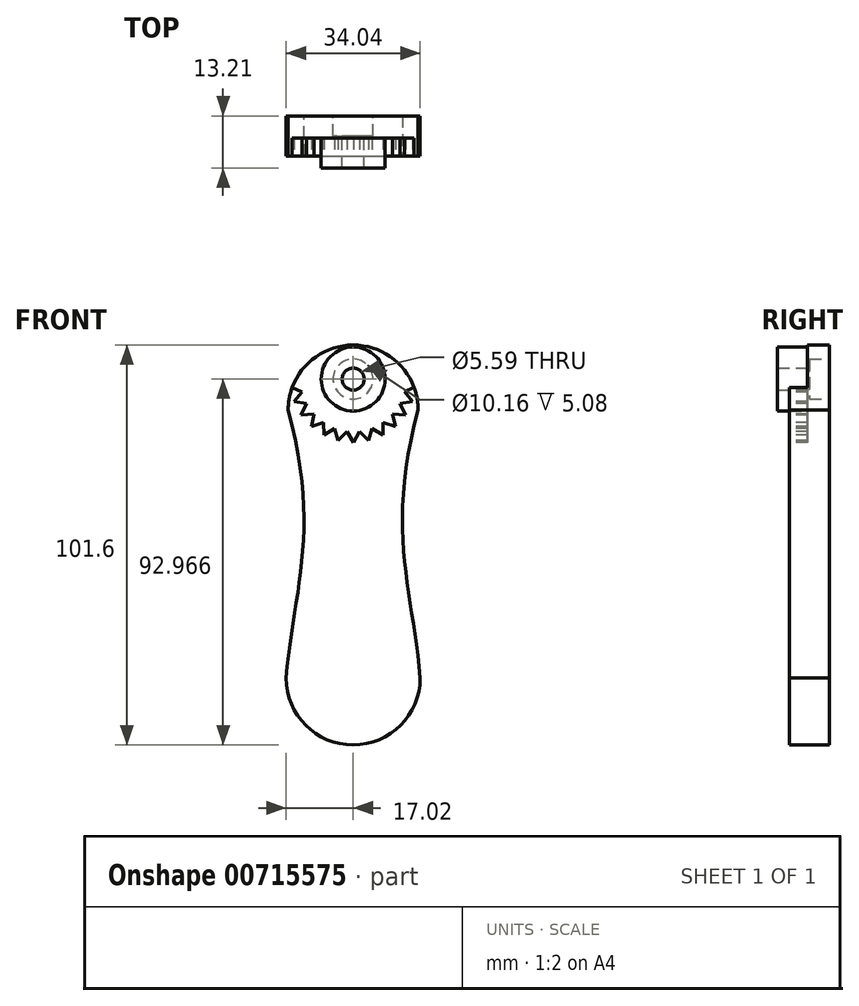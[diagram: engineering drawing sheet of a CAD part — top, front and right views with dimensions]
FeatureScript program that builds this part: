
annotation { "Feature Type Name" : "Feature", "Feature Type Description" : "" }
export const myFeature = defineFeature(function(context is Context, id is Id, definition is map)
    precondition{}
    {
        {
            var Q0;
            Q0=qCreatedBy(makeId("Front.planeOp"),FACE);
            var sketch = newSketch(context, id + "F0", { "sketchPlane" : qUnion([Q0])});
            skArc(sketch, "E0", {"start": v(16.51, 16.2) * mm, "mid": v(0, 32.71) * mm, "end": v(-16.51, 16.2) * mm});
            skArc(sketch, "E1", {"start": v(-17.02, -51.87) * mm, "mid": v(0, -68.89) * mm, "end": v(17.02, -51.87) * mm});
            skPoint(sketch, "E2", {"position": v(0, 32.71) * mm});
            skPoint(sketch, "E3", {"position": v(0, -68.89) * mm});
            skFitSpline(sketch, "E4", {"points": [v(-16.51, 16.2) * mm, v(-17.02, -51.87) * mm], "startDerivative": vector(24.94, -92.74) * mm, "endDerivative": vector(-5.66, -67.8) * mm});
            skFitSpline(sketch, "E5.MirrorCS", {"points": [v(16.51, 16.2) * mm, v(17.02, -51.87) * mm], "startDerivative": vector(-24.94, -92.74) * mm, "endDerivative": vector(5.66, -67.8) * mm});
            skLineSegment(sketch, "E6", {"start": v(-12.7, -17.82) * mm, "end": v(12.7, -17.82) * mm, "construction": true});
            skSolve(sketch);
        }
        {
            var Q0;
            Q0=makeQuery(id+"F0.imprint","IMPRINT",FACE,{"disambiguationData":[TD([[makeQuery(id+"F0.imprint","IMPRINT",EDGE,{"derivedFrom":sQuery(id+"F0.wireOp",EDGE,"E0")}),1.0]])]});
            extrude(context, id + "F1", {"entities" : qUnion([Q0]), "depth" : 10.16 * mm, "offsetDistance" : 25.4 * mm});
        }
        {
            var Q0;
            Q0=makeQuery(id+"F1.opExtrude","CAP_FACE",FACE,{"disambiguationData":[OSD([sQuery(id+"F0.wireOp",EDGE,"E0"),sQuery(id+"F0.wireOp",EDGE,"E1"),sQuery(id+"F0.wireOp",EDGE,"E4"),sQuery(id+"F0.wireOp",EDGE,"E5.MirrorCS")])],"isStart":false});
            var sketch = newSketch(context, id + "F2", { "sketchPlane" : qUnion([Q0])});
            skLineSegment(sketch, "E7", {"start": v(0, 32.71) * mm, "end": v(0, 24.08) * mm, "construction": true});
            skCircle(sketch, "E8", {"center": v(0, 24.08) * mm, "radius": 2.8 * mm});
            skCircle(sketch, "E9", {"center": v(0, 24.08) * mm, "radius": 8.13 * mm});
            skSolve(sketch);
        }
        {
            var Q0;
            Q0=makeQuery(id+"F2.imprint","IMPRINT",FACE,{"disambiguationData":[TD([[makeQuery(id+"F2.imprint","IMPRINT",EDGE,{"derivedFrom":sQuery(id+"F2.wireOp",EDGE,"E8")}),-1.0]])]});
            extrude(context, id + "F3", {"entities" : qUnion([Q0]), "operationType" : NewBodyOperationType.ADD, "depth" : 3.05 * mm, "offsetDistance" : 25.4 * mm});
        }
        {
            var Q0;
            Q0=makeQuery(id+"F3.boolean.opBoolean","SPLIT",FACE,{"disambiguationData":[TD([makeQuery(id+"F3.opExtrude","SWEPT_FACE",FACE,{"disambiguationData":[OSD([sQuery(id+"F2.wireOp",EDGE,"E8")])]})])],"derivedFrom":makeQuery(id+"F1.opExtrude","CAP_FACE",FACE,{"disambiguationData":[OSD([sQuery(id+"F0.wireOp",EDGE,"E0"),sQuery(id+"F0.wireOp",EDGE,"E1"),sQuery(id+"F0.wireOp",EDGE,"E4"),sQuery(id+"F0.wireOp",EDGE,"E5.MirrorCS")])],"isStart":false})});
            extrude(context, id + "F4", {"entities" : qUnion([Q0]), "operationType" : NewBodyOperationType.REMOVE, "endBound" : BoundingType.SYMMETRIC, "oppositeDirection" : true, "depth" : 101.6 * mm, "offsetDistance" : 25.4 * mm});
        }
        {
            var Q0;
            {var subQ0=sQuery(id+"F0.wireOp",EDGE,"E4");var subQ1=sQuery(id+"F0.wireOp",EDGE,"E1");var subQ2=sQuery(id+"F0.wireOp",EDGE,"E5.MirrorCS");var subQ3=sQuery(id+"F0.wireOp",EDGE,"E0");Q0=makeQuery(id+"F3.boolean.opBoolean","SPLIT",FACE,{"disambiguationData":[TD([makeQuery(id+"F1.opExtrude","SWEPT_FACE",FACE,{"disambiguationData":[OSD([subQ3])]})])],"derivedFrom":makeQuery(id+"F1.opExtrude","CAP_FACE",FACE,{"disambiguationData":[OSD([subQ3,subQ1,subQ0,subQ2])],"isStart":false})});}
            var sketch = newSketch(context, id + "F5", { "sketchPlane" : qUnion([Q0])});
            skLineSegment(sketch, "E10", {"start": v(0, 24.08) * mm, "end": v(0, 0) * mm, "construction": true});
            skLineSegment(sketch, "E11", {"start": v(-15.97, 22.08) * mm, "end": v(-12.93, 20.8) * mm});
            skLineSegment(sketch, "E12.1.0", {"start": v(-12.95, 20.88) * mm, "end": v(-15.03, 18.32) * mm});
            skLineSegment(sketch, "E12.1.1", {"start": v(-15.03, 18.32) * mm, "end": v(-11.77, 17.8) * mm});
            skLineSegment(sketch, "E12.2.0", {"start": v(-11.8, 17.88) * mm, "end": v(-13.21, 14.9) * mm});
            skLineSegment(sketch, "E12.2.1", {"start": v(-13.21, 14.9) * mm, "end": v(-9.92, 15.17) * mm});
            skLineSegment(sketch, "E12.3.0", {"start": v(-9.98, 15.23) * mm, "end": v(-10.63, 12) * mm});
            skLineSegment(sketch, "E12.3.1", {"start": v(-10.63, 12) * mm, "end": v(-7.5, 13.05) * mm});
            skLineSegment(sketch, "E12.4.0", {"start": v(-7.58, 13.1) * mm, "end": v(-7.43, 9.8) * mm});
            skLineSegment(sketch, "E12.4.1", {"start": v(-7.43, 9.8) * mm, "end": v(-4.65, 11.58) * mm});
            skLineSegment(sketch, "E12.5.0", {"start": v(-4.73, 11.6) * mm, "end": v(-3.8, 8.44) * mm});
            skLineSegment(sketch, "E12.5.1", {"start": v(-3.8, 8.44) * mm, "end": v(-1.52, 10.83) * mm});
            skLineSegment(sketch, "E12.6.0", {"start": v(-1.6, 10.84) * mm, "end": v(0.05, 7.98) * mm});
            skLineSegment(sketch, "E12.6.1", {"start": v(0.05, 7.98) * mm, "end": v(1.7, 10.85) * mm});
            skLineSegment(sketch, "E12.7.0", {"start": v(1.6, 10.84) * mm, "end": v(3.9, 8.46) * mm});
            skLineSegment(sketch, "E12.7.1", {"start": v(3.9, 8.46) * mm, "end": v(4.81, 11.64) * mm});
            skLineSegment(sketch, "E12.8.0", {"start": v(4.73, 11.6) * mm, "end": v(7.53, 9.85) * mm});
            skLineSegment(sketch, "E12.8.1", {"start": v(7.53, 9.85) * mm, "end": v(7.65, 13.15) * mm});
            skLineSegment(sketch, "E12.9.0", {"start": v(7.58, 13.1) * mm, "end": v(10.71, 12.07) * mm});
            skLineSegment(sketch, "E12.9.1", {"start": v(10.71, 12.07) * mm, "end": v(10.04, 15.3) * mm});
            skLineSegment(sketch, "E12.10.0", {"start": v(9.98, 15.23) * mm, "end": v(13.27, 14.98) * mm});
            skLineSegment(sketch, "E12.10.1", {"start": v(13.27, 14.98) * mm, "end": v(11.85, 17.96) * mm});
            skLineSegment(sketch, "E12.11.0", {"start": v(11.8, 17.88) * mm, "end": v(15.07, 18.42) * mm});
            skLineSegment(sketch, "E12.11.1", {"start": v(15.07, 18.42) * mm, "end": v(12.97, 20.97) * mm});
            skLineSegment(sketch, "E12.12.0", {"start": v(12.95, 20.88) * mm, "end": v(15.98, 22.19) * mm});
            skPoint(sketch, "E12.center", {"position": v(0, 24.08) * mm});
            skArc(sketch, "E13.trimOffspring", {"start": v(-13.33, 24.08) * mm, "mid": v(-13.33, 24.03) * mm, "end": v(-13.33, 23.99) * mm});
            skArc(sketch, "E14.trimOffspring", {"start": v(-12.95, 20.88) * mm, "mid": v(-12.94, 20.84) * mm, "end": v(-12.93, 20.8) * mm});
            skArc(sketch, "E15.trimOffspring", {"start": v(-11.8, 17.88) * mm, "mid": v(-11.79, 17.84) * mm, "end": v(-11.77, 17.8) * mm});
            skArc(sketch, "E16.trimOffspring", {"start": v(-9.98, 15.23) * mm, "mid": v(-9.95, 15.2) * mm, "end": v(-9.92, 15.17) * mm});
            skArc(sketch, "E17.trimOffspring", {"start": v(-7.58, 13.1) * mm, "mid": v(-7.54, 13.08) * mm, "end": v(-7.5, 13.05) * mm});
            skArc(sketch, "E18.trimOffspring", {"start": v(-4.73, 11.6) * mm, "mid": v(-4.69, 11.6) * mm, "end": v(-4.65, 11.58) * mm});
            skArc(sketch, "E19.trimOffspring", {"start": v(-1.6, 10.84) * mm, "mid": v(-1.56, 10.83) * mm, "end": v(-1.52, 10.83) * mm});
            skArc(sketch, "E20.trimOffspring", {"start": v(1.6, 10.84) * mm, "mid": v(1.65, 10.84) * mm, "end": v(1.7, 10.85) * mm});
            skArc(sketch, "E21.trimOffspring", {"start": v(4.73, 11.6) * mm, "mid": v(4.77, 11.62) * mm, "end": v(4.81, 11.64) * mm});
            skArc(sketch, "E22.trimOffspring", {"start": v(7.58, 13.1) * mm, "mid": v(7.61, 13.13) * mm, "end": v(7.65, 13.15) * mm});
            skArc(sketch, "E23.trimOffspring", {"start": v(11.8, 17.88) * mm, "mid": v(11.83, 17.92) * mm, "end": v(11.85, 17.96) * mm});
            skArc(sketch, "E24.trimOffspring", {"start": v(13.33, 24.08) * mm, "mid": v(13.33, 24.12) * mm, "end": v(13.33, 24.16) * mm});
            skArc(sketch, "E25.trimOffspring", {"start": v(12.95, 20.88) * mm, "mid": v(12.96, 20.93) * mm, "end": v(12.97, 20.97) * mm});
            skSolve(sketch);
        }
        {
            var Q0;
            Q0=qSketchRegion(id+"F5",true);
            var Q1;
            {var subQ49=sQuery(id+"F5.wireOp",EDGE,"E14.trimOffspring");Q1=makeQuery(id+"F5.imprint","IMPRINT",FACE,{"disambiguationData":[TD([[makeQuery(id+"F5.imprint","IMPRINT",EDGE,{"derivedFrom":subQ49}),1.0]])]});}
            extrude(context, id + "F6", {"entities" : qUnion([Q0, Q1]), "operationType" : NewBodyOperationType.REMOVE, "oppositeDirection" : true, "depth" : 4.57 * mm, "offsetDistance" : 25.4 * mm});
        }
        {
            var Q0;
            Q0=makeQuery(id+"F1.opExtrude","CAP_FACE",FACE,{"disambiguationData":[OSD([sQuery(id+"F0.wireOp",EDGE,"E0"),sQuery(id+"F0.wireOp",EDGE,"E1"),sQuery(id+"F0.wireOp",EDGE,"E4"),sQuery(id+"F0.wireOp",EDGE,"E5.MirrorCS")])],"isStart":true});
            var sketch = newSketch(context, id + "F7", { "sketchPlane" : qUnion([Q0])});
            skCircle(sketch, "E26.0", {"center": v(0, 24.08) * mm, "radius": 2.8 * mm});
            skCircle(sketch, "E27", {"center": v(0, 24.08) * mm, "radius": 5.08 * mm});
            skSolve(sketch);
        }
        {
            var Q0;
            Q0=makeQuery(id+"F7.imprint","IMPRINT",FACE,{"disambiguationData":[TD([[makeQuery(id+"F7.imprint","IMPRINT",EDGE,{"derivedFrom":sQuery(id+"F7.wireOp",EDGE,"E26.0")}),1.0]])]});
            extrude(context, id + "F8", {"entities" : qUnion([Q0]), "operationType" : NewBodyOperationType.REMOVE, "oppositeDirection" : true, "depth" : 5.08 * mm, "offsetDistance" : 25.4 * mm});
        }
    });
